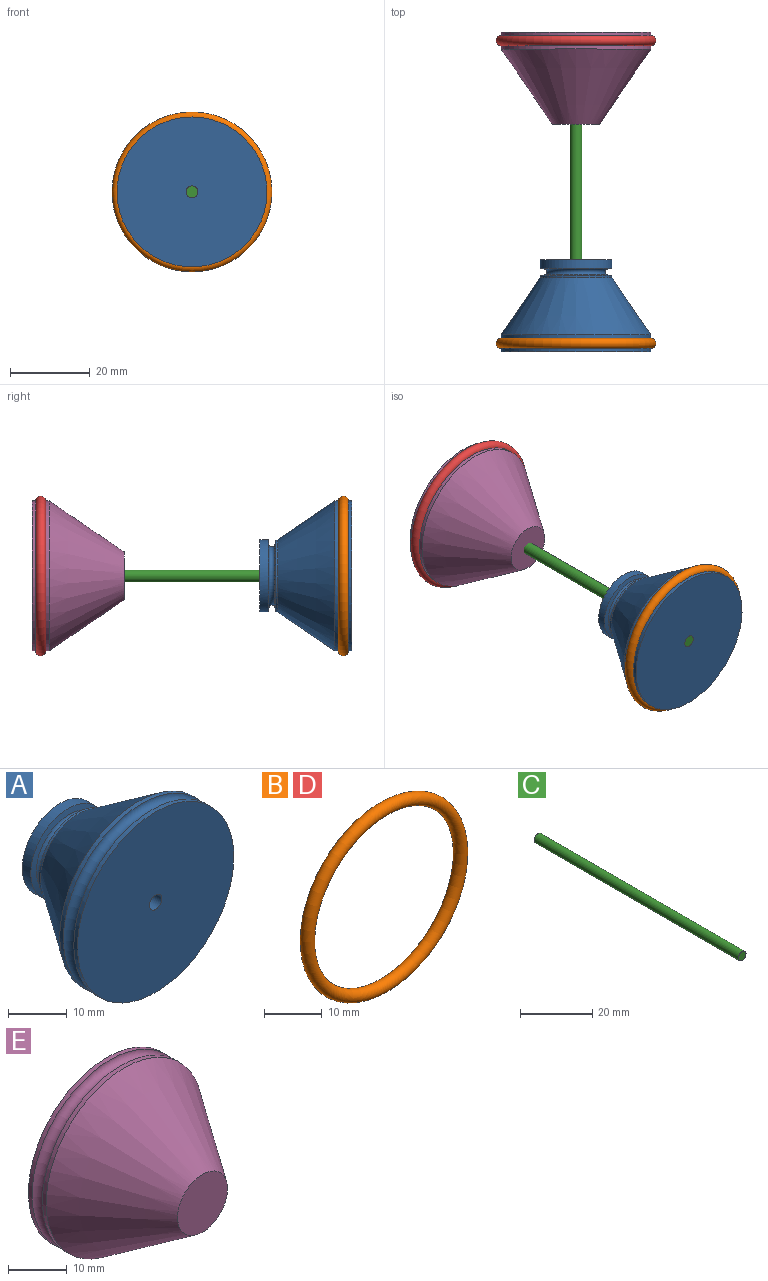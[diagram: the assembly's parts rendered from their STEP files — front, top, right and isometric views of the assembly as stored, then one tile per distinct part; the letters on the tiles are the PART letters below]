
ASSEMBLY  parts=5 mates=4
PART A: 12 faces, bbox 42.5x23x42.5 mm
  f0: torus R=18.75mm, axis (0,1,0), area 443mm2, adj f1,f4
  f1: cylinder r=18.75mm len=37.5mm, axis (0,1,0), area 103.1mm2, adj f0,f2
  f2: plane 37.5x37.5mm, normal (0,-1,0), area 1097.4mm2, adj f1,f11
  f3: cone r=18.75mm half-angle=34.2deg, axis (0,-1,0), area 1511.6mm2, adj f4,f5
  f4: cylinder r=18.75mm len=37.5mm, axis (0,1,0), area 103.1mm2, adj f0,f3
  f5: cylinder r=9mm len=18mm, axis (0,1,0), area 26.8mm2, adj f3,f8
  f6: cone r=7.87mm half-angle=80deg, axis (0,1,0), area 60.8mm2, adj f7,f10
  f7: torus R=8mm, axis (0,-1,0), area 98.3mm2, adj f6,f8
  f8: cone r=7.87mm half-angle=80deg, axis (0,-1,0), area 60.8mm2, adj f5,f7
  f9: plane 18x18mm, normal (0,1,0), area 247.4mm2, adj f10,f11
  f10: cylinder r=9mm len=18mm, axis (0,1,0), area 116.6mm2, adj f6,f9
  f11: cylinder r=1.5mm len=23mm, axis (0,-1,0), area 216.8mm2, adj f2,f9
PART B: 1 faces, bbox 43.3x2.5x43.3 mm
  f0: torus R=18.75mm, axis (0,-1,0), area 925.3mm2
PART C: 3 faces, bbox 3x80x3 mm
  f0: plane 3x3mm, normal (0,1,0), area 7.1mm2, adj f1
  f1: cylinder r=1.5mm len=80mm, axis (0,-1,0), area 754mm2, adj f0,f2
  f2: plane 3x3mm, normal (0,-1,0), area 7.1mm2, adj f1
PART D: same geometry as B
PART E: 6 faces, bbox 42.5x23x42.5 mm
  f0: plane 37.5x37.5mm, normal (0,1,0), area 1104.5mm2, adj f5
  f1: plane 12x12mm, normal (0,-1,0), area 113.1mm2, adj f2
  f2: cone r=18.75mm half-angle=34.2deg, axis (0,1,0), area 1763mm2, adj f1,f3
  f3: cylinder r=18.75mm len=37.5mm, axis (0,1,0), area 103.1mm2, adj f2,f4
  f4: torus R=18.75mm, axis (0,1,0), area 443mm2, adj f3,f5
  f5: cylinder r=18.75mm len=37.5mm, axis (0,1,0), area 103.1mm2, adj f0,f4
PLACE A at identity
PLACE B at identity
PLACE C at identity fixed
PLACE D t=(0,75.75,0)mm
PLACE E at identity
MATE fastened A.f0 <-> C.f1  axis (0,-1,0) through (-30,-40,20)mm
MATE fastened E.f2 <-> C.f1  axis (0,1,0) through (-30,40,20)mm
MATE fastened D.f0 <-> E.f2  axis (0,-1,0) through (-30,37.87,20)mm
MATE fastened A.f0 <-> B.f0  axis (0,1,0) through (-30,-37.88,20)mm
